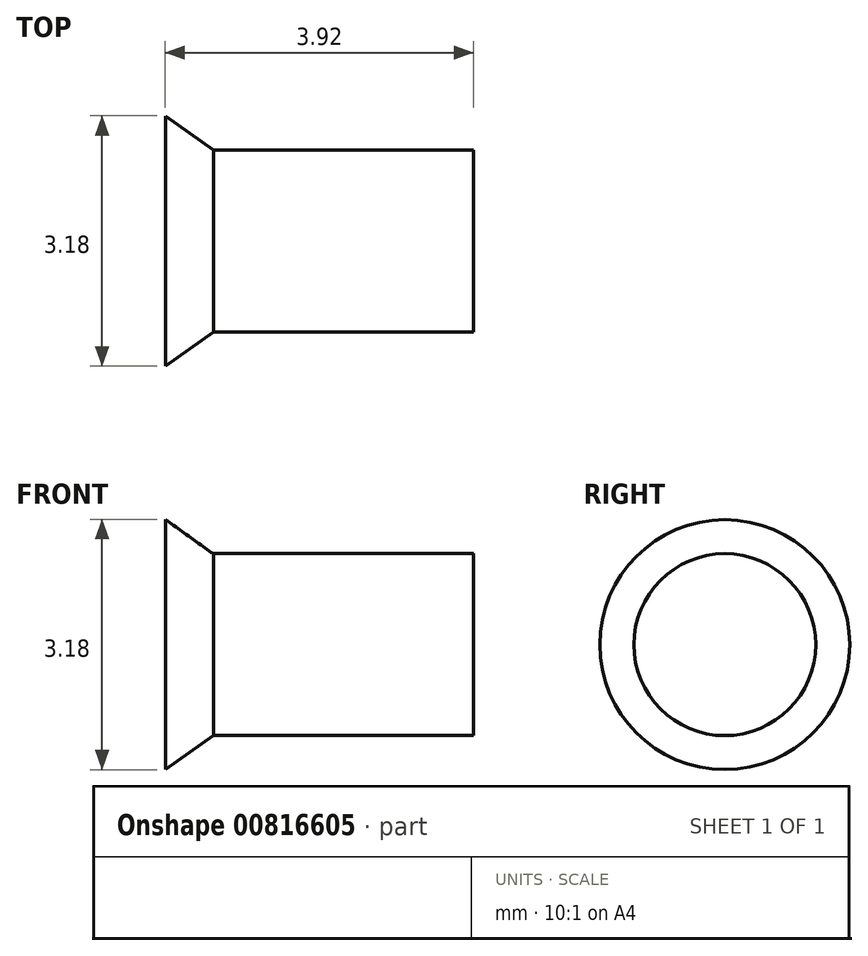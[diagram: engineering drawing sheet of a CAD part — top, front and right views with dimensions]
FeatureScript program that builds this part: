
annotation { "Feature Type Name" : "Feature", "Feature Type Description" : "" }
export const myFeature = defineFeature(function(context is Context, id is Id, definition is map)
    precondition{}
    {
        {
            var Q0;
            Q0=qCreatedBy(makeId("Front.planeOp"),FACE);
            var sketch = newSketch(context, id + "F0", { "sketchPlane" : qUnion([Q0])});
            skLineSegment(sketch, "E0", {"start": v(-1.96, 0) * mm, "end": v(1.96, 0) * mm});
            skLineSegment(sketch, "E1", {"start": v(1.96, 0) * mm, "end": v(1.96, 1.16) * mm});
            skLineSegment(sketch, "E2", {"start": v(1.96, 1.16) * mm, "end": v(-1.35, 1.16) * mm});
            skLineSegment(sketch, "E3", {"start": v(-1.35, 1.16) * mm, "end": v(-1.96, 1.59) * mm});
            skLineSegment(sketch, "E4", {"start": v(-1.96, 1.59) * mm, "end": v(-1.96, 0) * mm});
            skSolve(sketch);
        }
        {
            var Q0;
            Q0 = qSketchRegion(id + "F0", true);
            var Q1;
            Q1=sQuery(id+"F0.wireOp",EDGE,"E0");
            revolve(context, id + "F1", {"surfaceOperationType" : NewSurfaceOperationType.NEW, "entities" : qUnion([Q0]), "axis" : qUnion([Q1]), "revolveType" : RevolveType.FULL});
        }
    });
